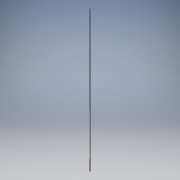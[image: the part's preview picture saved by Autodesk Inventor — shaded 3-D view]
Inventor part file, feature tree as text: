
AUTODESK INVENTOR PART (.ipt)
format: ipt  version: 2016 (Build 200138000, 138)  size: 161,792 bytes
history: native  units: mm
features: other x2, sheet_metal_op x2, sketch x2, chamfer x1, extrude x1, pattern_linear x1
ambient origin geometry x8: Origin, YZ Plane, XZ Plane, XY Plane, X Axis, Y Axis, Z Axis, Center Point
bodies: Solid1 (feature_tree)
feature tree (9):
  parser-record x1  (decoder bookkeeping rows leaked as tree rows — omitted from the tree; the rows remain in map.json)
  sheet_metal_op  "Contour Flange1"
  chamfer  "Corner Round1"
  extrude  "Extrusion1"  Depth=20.0mm
  pattern_linear  "Rectangular Pattern1"  Spacing1=3.0mm  [1 undecoded]
  sketch  "Sketch1"  dims[d0=20.0mm d1=20.0mm]
  other  "Plate1"
  sheet_metal_op  "Bend1"
  sketch  "Sketch2"  dims[d2=44.0mm d3=3.0mm d4=1.5mm d5=6.0mm d6=3.0mm d8=3.0mm d9=3.0mm d10=12.0mm d11=3.0mm d12=3.0mm d13=6.0mm d16=9.525mm d18=9.525mm d19=9.525mm d21=10.0mm d22=0.0mm d23=20.0mm d25=448.6275mm]
note: 1 required parameter value undecoded (feature->parameter linkage not recoverable at this tier; creation-order binding heuristic only, values carry confidence <= 0.55)
note: 1 file-system path scrubbed to <path> (originals preserved in map.json)
